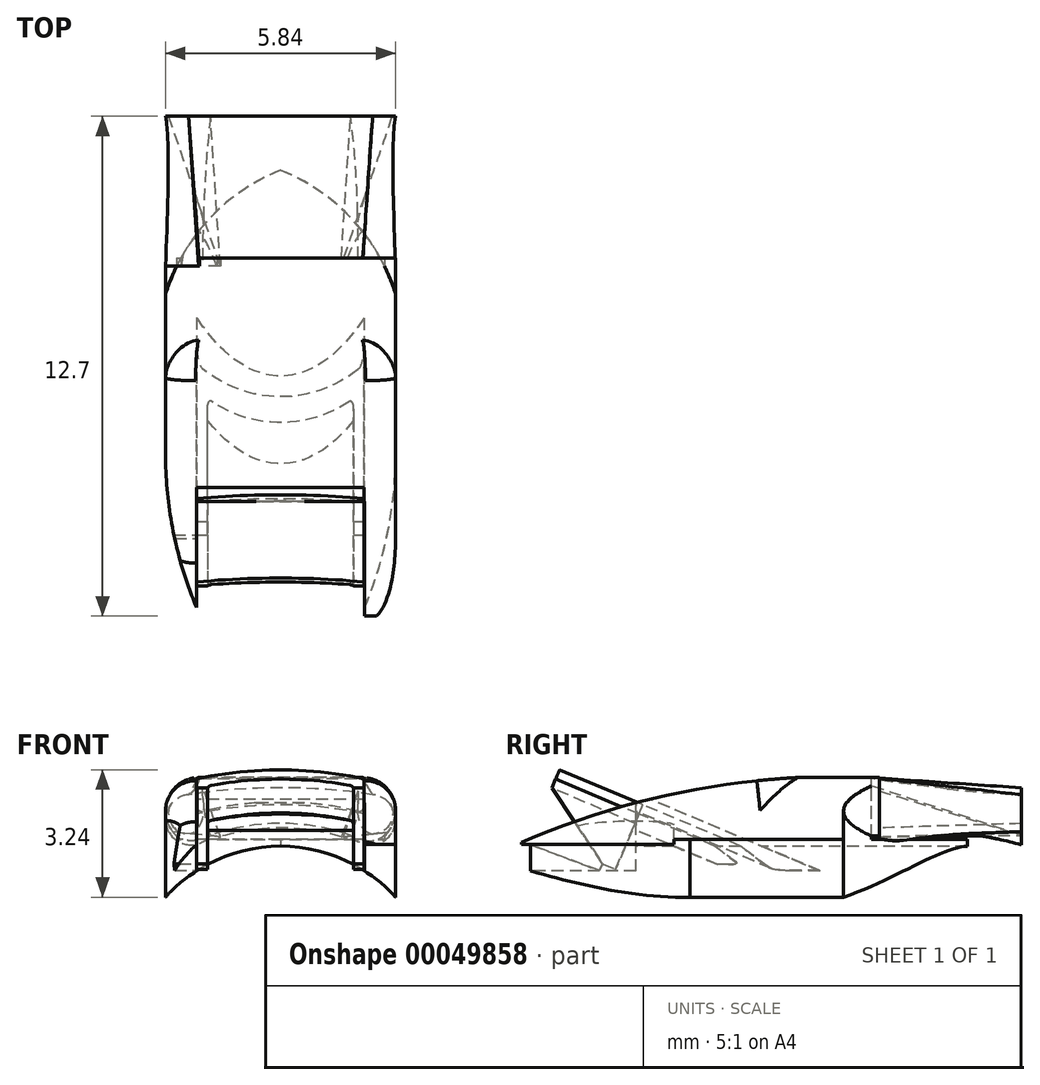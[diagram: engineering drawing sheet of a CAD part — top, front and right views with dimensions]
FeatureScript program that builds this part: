
annotation { "Feature Type Name" : "Feature", "Feature Type Description" : "" }
export const myFeature = defineFeature(function(context is Context, id is Id, definition is map)
    precondition{}
    {
        {
            var Q0;
            Q0=qCreatedBy(makeId("Front.planeOp"),FACE);
            var sketch = newSketch(context, id + "F0", { "sketchPlane" : qUnion([Q0])});
            skCircle(sketch, "E0", {"center": v(0, 0) * mm, "radius": 3.94 * mm});
            skSolve(sketch);
        }
        {
            var Q0;
            Q0=qCreatedBy(makeId("Top.planeOp"),FACE);
            cPlane(context, id + "F1", {"entities" : qUnion([Q0]), "cplaneType" : CPlaneType.OFFSET, "offset" : 2.84 * mm, "width" : 152.4 * mm, "height" : 152.4 * mm});
        }
        {
            var Q0;
            Q0=qCreatedBy(id+"F1.planeOp",FACE);
            var sketch = newSketch(context, id + "F2", { "sketchPlane" : qUnion([Q0])});
            skLineSegment(sketch, "E1", {"start": v(-2.04, 0) * mm, "end": v(2.04, 0) * mm});
            skLineSegment(sketch, "E2", {"start": v(0, 8.17) * mm, "end": v(0, 11.33) * mm});
            skArc(sketch, "E3", {"start": v(0, 11.33) * mm, "mid": v(-1.82, 10.09) * mm, "end": v(-2.92, 8.17) * mm});
            skArc(sketch, "E4.MirrorCS", {"start": v(0, 11.33) * mm, "mid": v(1.82, 10.09) * mm, "end": v(2.92, 8.17) * mm});
            skArc(sketch, "E5", {"start": v(-2.92, 4.28) * mm, "mid": v(-2.71, 2.1) * mm, "end": v(-2.04, 0) * mm});
            skArc(sketch, "E6.MirrorCS", {"start": v(2.92, 4.28) * mm, "mid": v(2.71, 2.1) * mm, "end": v(2.04, 0) * mm});
            skLineSegment(sketch, "E7", {"start": v(-2.92, 4.28) * mm, "end": v(-2.92, 8.17) * mm});
            skLineSegment(sketch, "E8", {"start": v(2.92, 4.28) * mm, "end": v(2.92, 8.17) * mm});
            skSolve(sketch);
        }
        {
            var Q0;
            Q0 = qSketchRegion(id + "F2", true);
            extrude(context, id + "F3", {"entities" : qUnion([Q0]), "depth" : 1.27 * mm, "offsetDistance" : 25.4 * mm});
        }
        {
            var Q0;
            Q0=qCreatedBy(makeId("Front.planeOp"),FACE);
            var sketch = newSketch(context, id + "F4", { "sketchPlane" : qUnion([Q0])});
            skLineSegment(sketch, "E9.bottom", {"start": v(2.92, 3.98) * mm, "end": v(-2.92, 3.98) * mm});
            skLineSegment(sketch, "E9.top", {"start": v(2.92, 5.68) * mm, "end": v(-2.92, 5.68) * mm});
            skLineSegment(sketch, "E9.left", {"start": v(2.92, 3.98) * mm, "end": v(2.92, 5.68) * mm});
            skLineSegment(sketch, "E9.right", {"start": v(-2.92, 3.98) * mm, "end": v(-2.92, 5.68) * mm});
            skPoint(sketch, "E9.middle", {"position": v(0, 4.83) * mm});
            skLineSegment(sketch, "E10", {"start": v(0, 3.98) * mm, "end": v(0, 2.84) * mm});
            skSolve(sketch);
        }
        {
            var Q0;
            Q0 = qSketchRegion(id + "F4", true);
            extrude(context, id + "F5", {"entities" : qUnion([Q0]), "oppositeDirection" : true, "depth" : 8.9 * mm, "offsetDistance" : 25.4 * mm});
        }
        {
            var Q0;
            Q0=makeQuery(id+"F5.opExtrude","CAP_FACE",FACE,{"disambiguationData":[OSD([sQuery(id+"F4.wireOp",EDGE,"E9.bottom"),sQuery(id+"F4.wireOp",EDGE,"E9.top"),sQuery(id+"F4.wireOp",EDGE,"E9.left"),sQuery(id+"F4.wireOp",EDGE,"E9.right")])],"isStart":false});
            var sketch = newSketch(context, id + "F6", { "sketchPlane" : qUnion([Q0])});
            skLineSegment(sketch, "E11.bottom", {"start": v(2.92, 3.98) * mm, "end": v(-2.92, 3.98) * mm});
            skLineSegment(sketch, "E11.top", {"start": v(2.92, 5.68) * mm, "end": v(-2.92, 5.68) * mm});
            skLineSegment(sketch, "E11.left", {"start": v(2.92, 3.98) * mm, "end": v(2.92, 5.68) * mm});
            skLineSegment(sketch, "E11.right", {"start": v(-2.92, 3.98) * mm, "end": v(-2.92, 5.68) * mm});
            skPoint(sketch, "E11.middle", {"position": v(0, 4.83) * mm});
            skLineSegment(sketch, "E12", {"start": v(0, 3.98) * mm, "end": v(0, 2.84) * mm});
            skLineSegment(sketch, "E13", {"start": v(-2.92, 4.83) * mm, "end": v(-4.23, 4.85) * mm});
            skLineSegment(sketch, "E14", {"start": v(-2.92, 3.98) * mm, "end": v(-3.64, 3.98) * mm});
            skLineSegment(sketch, "E15", {"start": v(-3.64, 3.98) * mm, "end": v(-3.64, 4.84) * mm});
            skLineSegment(sketch, "E16", {"start": v(-3.64, 4.4) * mm, "end": v(-3.33, 4.4) * mm});
            skLineSegment(sketch, "E17", {"start": v(-3.33, 4.4) * mm, "end": v(-3.33, 3.98) * mm});
            skLineSegment(sketch, "E18", {"start": v(-2.92, 5.68) * mm, "end": v(-3.33, 5.68) * mm});
            skLineSegment(sketch, "E19", {"start": v(-2.34, 5.68) * mm, "end": v(-2.34, 5.68) * mm});
            skArc(sketch, "E20", {"start": v(-2.06, 5.68) * mm, "mid": v(-2.87, 4.54) * mm, "end": v(-1.53, 4.17) * mm});
            skArc(sketch, "E21", {"start": v(1.53, 4.17) * mm, "mid": v(2.87, 4.54) * mm, "end": v(2.06, 5.68) * mm});
            skArc(sketch, "E22", {"start": v(1.53, 4.17) * mm, "mid": v(0, 4.4) * mm, "end": v(-1.53, 4.17) * mm});
            skLineSegment(sketch, "E23", {"start": v(1.53, 4.17) * mm, "end": v(2.06, 5.68) * mm});
            skLineSegment(sketch, "E24", {"start": v(-1.53, 4.17) * mm, "end": v(-2.06, 5.68) * mm});
            skSolve(sketch);
        }
        {
            var Q0;
            Q0=makeQuery(id+"F2.imprint","IMPRINT",FACE,{"disambiguationData":[TD([[makeQuery(id+"F2.imprint","IMPRINT",EDGE,{"derivedFrom":sQuery(id+"F2.wireOp",EDGE,"E1")}),1.0]])]});
            extrude(context, id + "F7", {"entities" : qUnion([Q0]), "operationType" : NewBodyOperationType.ADD, "oppositeDirection" : true, "depth" : 0.25 * mm, "offsetDistance" : 25.4 * mm});
        }
        {
            var Q0;
            Q0=qCreatedBy(makeId("Front.planeOp"),FACE);
            cPlane(context, id + "F8", {"entities" : qUnion([Q0]), "cplaneType" : CPlaneType.OFFSET, "offset" : 12.7 * mm, "oppositeDirection" : true, "width" : 152.4 * mm, "height" : 152.4 * mm});
        }
        {
            var Q0;
            Q0=qCreatedBy(id+"F8.planeOp",FACE);
            var sketch = newSketch(context, id + "F9", { "sketchPlane" : qUnion([Q0])});
            skArc(sketch, "E25", {"start": v(-2.34, 5.24) * mm, "mid": v(-2.84, 4.3) * mm, "end": v(-1.78, 4.21) * mm});
            skArc(sketch, "E26.MirrorC", {"start": v(2.41, 5.23) * mm, "mid": v(2.82, 4.27) * mm, "end": v(1.78, 4.21) * mm});
            skArc(sketch, "E27", {"start": v(1.78, 4.21) * mm, "mid": v(0, 4.51) * mm, "end": v(-1.78, 4.21) * mm});
            skLineSegment(sketch, "E28", {"start": v(0, 4.51) * mm, "end": v(0, 3.97) * mm});
            skArc(sketch, "E29", {"start": v(2.41, 5.23) * mm, "mid": v(0.04, 5.42) * mm, "end": v(-2.34, 5.24) * mm});
            skLineSegment(sketch, "E30", {"start": v(-1.78, 4.21) * mm, "end": v(-2.34, 5.24) * mm});
            skLineSegment(sketch, "E31", {"start": v(1.78, 4.21) * mm, "end": v(2.41, 5.23) * mm});
            skSolve(sketch);
        }
        {
            var Q0;
            {var subQ5=sQuery(id+"F6.wireOp",EDGE,"E23");Q0=makeQuery(id+"F6.imprint","IMPRINT",FACE,{"disambiguationData":[TD([[makeQuery(id+"F6.imprint","IMPRINT",EDGE,{"derivedFrom":subQ5}),-1.0]])]});}
            var Q1;
            Q1=makeQuery(id+"F9.imprint","IMPRINT",FACE,{"disambiguationData":[TD([[makeQuery(id+"F9.imprint","IMPRINT",EDGE,{"derivedFrom":sQuery(id+"F9.wireOp",EDGE,"E25")}),1.0]])]});
            loft(context, id + "F10", {"sheetProfilesArray" : [{ "sheetProfileEntities" : qUnion([Q0]) }, { "sheetProfileEntities" : qUnion([Q1]) }]});
        }
        {
            var Q0;
            Q0=makeQuery(id+"F6.imprint","IMPRINT",FACE,{"disambiguationData":[TD([[makeQuery(id+"F6.imprint","IMPRINT",EDGE,{"derivedFrom":sQuery(id+"F6.wireOp",EDGE,"E22")}),-1.0]])]});
            var Q1;
            Q1=makeQuery(id+"F9.imprint","IMPRINT",FACE,{"disambiguationData":[TD([[makeQuery(id+"F9.imprint","IMPRINT",EDGE,{"derivedFrom":sQuery(id+"F9.wireOp",EDGE,"E29")}),1.0]])]});
            loft(context, id + "F11", {"sheetProfilesArray" : [{ "sheetProfileEntities" : qUnion([Q0]) }, { "sheetProfileEntities" : qUnion([Q1]) }]});
        }
        {
            var Q0;
            {var subQ5=sQuery(id+"F6.wireOp",EDGE,"E23");Q0=makeQuery(id+"F10.opLoft","SWEPT_BODY",BODY,{"disambiguationData":[OSD([makeQuery(id+"F6.imprint","IMPRINT",FACE,{"disambiguationData":[TD([[makeQuery(id+"F6.imprint","IMPRINT",EDGE,{"derivedFrom":subQ5}),-1.0]])]}),makeQuery(id+"F9.imprint","IMPRINT",FACE,{"disambiguationData":[TD([[makeQuery(id+"F9.imprint","IMPRINT",EDGE,{"derivedFrom":sQuery(id+"F9.wireOp",EDGE,"E25")}),1.0]])]})])]});}
            var Q1;
            Q1=qCreatedBy(makeId("Right.planeOp"),FACE);
            mirror(context, id + "F12", {"entities" : qUnion([Q0]), "mirrorPlane" : qUnion([Q1])});
        }
        {
            var Q0;
            Q0=qCreatedBy(makeId("Right.planeOp"),FACE);
            var sketch = newSketch(context, id + "F13", { "sketchPlane" : qUnion([Q0])});
            skArc(sketch, "E32", {"start": v(8.87, 5.7) * mm, "mid": v(4.34, 5.36) * mm, "end": v(0, 4.03) * mm});
            skLineSegment(sketch, "E33", {"start": v(8.87, 5.7) * mm, "end": v(-0.3, 5.7) * mm});
            skLineSegment(sketch, "E34", {"start": v(-0.3, 5.7) * mm, "end": v(-0.3, 4.03) * mm});
            skLineSegment(sketch, "E35", {"start": v(-0.3, 4.03) * mm, "end": v(0, 4.03) * mm});
            skSolve(sketch);
        }
        {
            var Q0;
            Q0 = qSketchRegion(id + "F13", true);
            extrude(context, id + "F14", {"entities" : qUnion([Q0]), "operationType" : NewBodyOperationType.REMOVE, "depth" : 25.4 * mm, "offsetDistance" : 25.4 * mm, "symmetric" : true});
        }
        {
            var Q0;
            Q0=makeQuery(id+"F5.opExtrude","SWEPT_FACE",FACE,{"disambiguationData":[OSD([sQuery(id+"F4.wireOp",EDGE,"E9.top")])]});
            var sketch = newSketch(context, id + "F15", { "sketchPlane" : qUnion([Q0])});
            skArc(sketch, "E36", {"start": v(-2.64, 8.9) * mm, "mid": v(-2.8, 8.54) * mm, "end": v(-2.92, 8.17) * mm});
            skArc(sketch, "E37.MirrorCS", {"start": v(2.64, 8.89) * mm, "mid": v(2.8, 8.54) * mm, "end": v(2.92, 8.17) * mm});
            skArc(sketch, "E38", {"start": v(-2.92, 4.28) * mm, "mid": v(-2.71, 2.1) * mm, "end": v(-2.04, 0) * mm});
            skArc(sketch, "E39.MirrorCS", {"start": v(2.92, 4.28) * mm, "mid": v(2.71, 2.1) * mm, "end": v(2.04, 0) * mm});
            skLineSegment(sketch, "E40", {"start": v(2.92, 4.28) * mm, "end": v(3.2, 4.17) * mm});
            skLineSegment(sketch, "E41", {"start": v(3.2, 4.17) * mm, "end": v(3.2, -0.35) * mm});
            skLineSegment(sketch, "E42", {"start": v(3.2, -0.35) * mm, "end": v(2.04, -0.35) * mm});
            skLineSegment(sketch, "E43", {"start": v(2.04, -0.35) * mm, "end": v(2.04, 0) * mm});
            skLineSegment(sketch, "E44", {"start": v(-2.92, 4.28) * mm, "end": v(-3.5, 4.28) * mm});
            skLineSegment(sketch, "E45", {"start": v(-3.5, 4.28) * mm, "end": v(-3.5, -0.35) * mm});
            skLineSegment(sketch, "E46", {"start": v(-3.5, -0.35) * mm, "end": v(-2.04, -0.35) * mm});
            skLineSegment(sketch, "E47", {"start": v(-2.04, -0.35) * mm, "end": v(-2.04, 0) * mm});
            skLineSegment(sketch, "E48", {"start": v(2.64, 8.9) * mm, "end": v(2.92, 8.9) * mm});
            skLineSegment(sketch, "E49", {"start": v(2.92, 8.9) * mm, "end": v(2.92, 8.17) * mm});
            skLineSegment(sketch, "E50", {"start": v(-2.64, 8.9) * mm, "end": v(-2.92, 8.9) * mm});
            skLineSegment(sketch, "E51", {"start": v(-2.92, 8.9) * mm, "end": v(-2.92, 8.17) * mm});
            skSolve(sketch);
        }
        {
            var Q0;
            Q0=makeQuery(id+"F15.imprint","IMPRINT",FACE,{"disambiguationData":[TD([[makeQuery(id+"F15.imprint","IMPRINT",EDGE,{"derivedFrom":sQuery(id+"F15.wireOp",EDGE,"E38")}),-1.0]])]});
            var Q1;
            Q1=makeQuery(id+"F15.imprint","IMPRINT",FACE,{"disambiguationData":[TD([[makeQuery(id+"F15.imprint","IMPRINT",EDGE,{"derivedFrom":sQuery(id+"F15.wireOp",EDGE,"E39.MirrorCS")}),1.0]])]});
            var Q2;
            {var subQ0=sQuery(id+"F15.wireOp",EDGE,"E51");Q2=makeQuery(id+"F15.imprint","IMPRINT",FACE,{"disambiguationData":[TD([[makeQuery(id+"F15.imprint","IMPRINT",EDGE,{"derivedFrom":subQ0}),1.0]])]});}
            var Q3;
            {var subQ0=sQuery(id+"F15.wireOp",EDGE,"E49");Q3=makeQuery(id+"F15.imprint","IMPRINT",FACE,{"disambiguationData":[TD([[makeQuery(id+"F15.imprint","IMPRINT",EDGE,{"derivedFrom":subQ0}),-1.0]])]});}
            extrude(context, id + "F16", {"entities" : qUnion([Q0, Q1, Q2, Q3]), "operationType" : NewBodyOperationType.REMOVE, "oppositeDirection" : true, "depth" : 1.78 * mm, "offsetDistance" : 25.4 * mm});
        }
        {
            var Q0;
            Q0=makeQuery(id+"F0.imprint","IMPRINT",FACE,{"disambiguationData":[TD([[makeQuery(id+"F0.imprint","IMPRINT",EDGE,{"derivedFrom":sQuery(id+"F0.wireOp",EDGE,"E0")}),1.0]])]});
            extrude(context, id + "F17", {"entities" : qUnion([Q0]), "operationType" : NewBodyOperationType.REMOVE, "oppositeDirection" : true, "depth" : 25.4 * mm, "offsetDistance" : 25.4 * mm});
        }
        {
            var Q0;
            Q0=makeQuery(id+"F5.opExtrude","SWEPT_EDGE",EDGE,{"disambiguationData":[OSD([sQuery(id+"F4.wireOp",EDGE,"E9.top"),sQuery(id+"F4.wireOp",EDGE,"E9.right")])]});
            var Q1;
            Q1=makeQuery(id+"F5.opExtrude","SWEPT_EDGE",EDGE,{"disambiguationData":[OSD([sQuery(id+"F4.wireOp",EDGE,"E9.top"),sQuery(id+"F4.wireOp",EDGE,"E9.left")])]});
            fillet(context, id + "F18", {"entities" : qUnion([Q0, Q1]), "tangentPropagation" : true, "radius" : 0.84 * mm, "defaultsChanged" : false, "vertexSettings" : [], "allowEdgeOverflow" : false});
        }
        {
            var Q0;
            {var subQ0=sQuery(id+"F4.wireOp",EDGE,"E9.right");var subQ2=sQuery(id+"F4.wireOp",EDGE,"E9.top");var subQ3=sQuery(id+"F13.wireOp",EDGE,"E32");Q0=makeQuery(id+"F18.opFillet","BLEND_EDGE",EDGE,{"blendedFrom":[makeQuery(id+"F5.opExtrude","SWEPT_EDGE",EDGE,{"disambiguationData":[OSD([subQ2,subQ0])]}),makeQuery(id+"F14.boolean.opBoolean","COPY",FACE,{"disambiguationData":[TD([makeQuery(id+"F5.opExtrude","SWEPT_FACE",FACE,{"disambiguationData":[OSD([subQ2])]})])],"derivedFrom":makeQuery(id+"F14.opExtrude","SWEPT_FACE",FACE,{"disambiguationData":[OSD([subQ3]),TDD([makeQuery(id+"F13.imprint","IMPRINT",EDGE,{"disambiguationData":[TD([[makeQuery(id+"F13.imprint","INTERSECT",VERTEX,{"derivedFrom":[subQ3,sQuery(id+"F13.wireOp",EDGE,"E35")]}),1.0]])],"derivedFrom":subQ3})])]})})],"blendedInto":[makeQuery(id+"F14.boolean.opBoolean","COPY",FACE,{"disambiguationData":[TD([makeQuery(id+"F5.opExtrude","SWEPT_FACE",FACE,{"disambiguationData":[OSD([subQ2])]})])],"derivedFrom":makeQuery(id+"F14.opExtrude","SWEPT_FACE",FACE,{"disambiguationData":[OSD([subQ3]),TDD([makeQuery(id+"F13.imprint","IMPRINT",EDGE,{"disambiguationData":[TD([[makeQuery(id+"F13.imprint","INTERSECT",VERTEX,{"derivedFrom":[subQ3,sQuery(id+"F13.wireOp",EDGE,"E35")]}),1.0]])],"derivedFrom":subQ3})])]})})]});}
            fillet(context, id + "F19", {"entities" : qUnion([Q0]), "tangentPropagation" : true, "radius" : 0.76 * mm, "defaultsChanged" : true, "vertexSettings" : [], "allowEdgeOverflow" : false});
        }
        {
            var Q0;
            Q0=makeQuery(id+"F5.opExtrude","SWEPT_FACE",FACE,{"disambiguationData":[OSD([sQuery(id+"F4.wireOp",EDGE,"E9.bottom")])]});
            var sketch = newSketch(context, id + "F20", { "sketchPlane" : qUnion([Q0])});
            skArc(sketch, "E52", {"start": v(2.64, -8.89) * mm, "mid": v(2.8, -8.54) * mm, "end": v(2.92, -8.17) * mm});
            skArc(sketch, "E53.MirrorCS", {"start": v(-2.64, -8.89) * mm, "mid": v(-2.8, -8.54) * mm, "end": v(-2.92, -8.17) * mm});
            skLineSegment(sketch, "E54", {"start": v(-2.64, -8.89) * mm, "end": v(-2.92, -8.89) * mm});
            skLineSegment(sketch, "E55", {"start": v(-2.92, -8.89) * mm, "end": v(-2.92, -8.17) * mm});
            skLineSegment(sketch, "E56", {"start": v(2.64, -8.89) * mm, "end": v(2.92, -8.89) * mm});
            skLineSegment(sketch, "E57", {"start": v(2.92, -8.89) * mm, "end": v(2.92, -8.17) * mm});
            skSolve(sketch);
        }
        {
            var Q0;
            {var subQ0=sQuery(id+"F20.wireOp",EDGE,"E56");Q0=makeQuery(id+"F20.imprint","IMPRINT",FACE,{"disambiguationData":[TD([[makeQuery(id+"F20.imprint","IMPRINT",EDGE,{"derivedFrom":subQ0}),1.0]])]});}
            var Q1;
            {var subQ0=sQuery(id+"F20.wireOp",EDGE,"E54");Q1=makeQuery(id+"F20.imprint","IMPRINT",FACE,{"disambiguationData":[TD([[makeQuery(id+"F20.imprint","IMPRINT",EDGE,{"derivedFrom":subQ0}),-1.0]])]});}
            extrude(context, id + "F21", {"entities" : qUnion([Q0, Q1]), "operationType" : NewBodyOperationType.REMOVE, "oppositeDirection" : true, "depth" : 2.74 * mm, "offsetDistance" : 25.4 * mm});
        }
        {
            var Q0;
            {var subQ5=sQuery(id+"F6.wireOp",EDGE,"E23");Q0=makeQuery(id+"F6.imprint","IMPRINT",FACE,{"disambiguationData":[TD([[makeQuery(id+"F6.imprint","IMPRINT",EDGE,{"derivedFrom":subQ5}),-1.0]])]});}
            var Q1;
            {var subQ0=sQuery(id+"F6.wireOp",EDGE,"E24");Q1=makeQuery(id+"F6.imprint","IMPRINT",FACE,{"disambiguationData":[TD([[makeQuery(id+"F6.imprint","IMPRINT",EDGE,{"derivedFrom":subQ0}),1.0]])]});}
            extrude(context, id + "F22", {"entities" : qUnion([Q0, Q1]), "oppositeDirection" : true, "depth" : 1.27 * mm, "offsetDistance" : 25.4 * mm});
        }
        {
            var Q0;
            Q0=makeQuery(id+"F3.opExtrude","SWEPT_BODY",BODY,{"disambiguationData":[OSD([sQuery(id+"F2.wireOp",EDGE,"E1"),sQuery(id+"F2.wireOp",EDGE,"E3"),sQuery(id+"F2.wireOp",EDGE,"E4.MirrorCS"),sQuery(id+"F2.wireOp",EDGE,"E5"),sQuery(id+"F2.wireOp",EDGE,"E6.MirrorCS"),sQuery(id+"F2.wireOp",EDGE,"E7"),sQuery(id+"F2.wireOp",EDGE,"E8")])]});
            var Q1;
            Q1=makeQuery(id+"F5.opExtrude","SWEPT_BODY",BODY,{"disambiguationData":[OSD([sQuery(id+"F4.wireOp",EDGE,"E9.bottom"),sQuery(id+"F4.wireOp",EDGE,"E9.top"),sQuery(id+"F4.wireOp",EDGE,"E9.left"),sQuery(id+"F4.wireOp",EDGE,"E9.right")])]});
            var Q2;
            Q2=makeQuery(id+"F22.opExtrude","SWEPT_BODY",BODY,{"disambiguationData":[OSD([sQuery(id+"F6.wireOp",EDGE,"E11.top"),sQuery(id+"F6.wireOp",EDGE,"E20"),sQuery(id+"F6.wireOp",EDGE,"E24")])]});
            var Q3;
            {var subQ5=sQuery(id+"F6.wireOp",EDGE,"E23");Q3=makeQuery(id+"F10.opLoft","SWEPT_BODY",BODY,{"disambiguationData":[OSD([makeQuery(id+"F6.imprint","IMPRINT",FACE,{"disambiguationData":[TD([[makeQuery(id+"F6.imprint","IMPRINT",EDGE,{"derivedFrom":subQ5}),-1.0]])]}),makeQuery(id+"F9.imprint","IMPRINT",FACE,{"disambiguationData":[TD([[makeQuery(id+"F9.imprint","IMPRINT",EDGE,{"derivedFrom":sQuery(id+"F9.wireOp",EDGE,"E25")}),1.0]])]})])]});}
            var Q4;
            Q4=makeQuery(id+"F22.opExtrude","SWEPT_BODY",BODY,{"disambiguationData":[OSD([sQuery(id+"F6.wireOp",EDGE,"E11.top"),sQuery(id+"F6.wireOp",EDGE,"E21"),sQuery(id+"F6.wireOp",EDGE,"E23")])]});
            booleanBodies(context, id + "F23", {"operationType" : BooleanOperationType.UNION, "tools" : qUnion([Q0, Q1, Q2, Q3, Q4])});
        }
        {
            var Q0;
            Q0=makeQuery(id+"F5.opExtrude","SWEPT_FACE",FACE,{"disambiguationData":[OSD([sQuery(id+"F4.wireOp",EDGE,"E9.top")])]});
            var sketch = newSketch(context, id + "F24", { "sketchPlane" : qUnion([Q0])});
            skLineSegment(sketch, "E58", {"start": v(-2.14, 2.9) * mm, "end": v(-2.14, 0) * mm});
            skLineSegment(sketch, "E59.MirrorCS", {"start": v(2.14, 2.9) * mm, "end": v(2.14, 0) * mm});
            skLineSegment(sketch, "E60", {"start": v(-2.14, 0) * mm, "end": v(2.14, 0) * mm});
            skLineSegment(sketch, "E61", {"start": v(-2.14, 2.9) * mm, "end": v(2.14, 2.9) * mm});
            skSolve(sketch);
        }
        {
            var Q0;
            Q0 = qSketchRegion(id + "F24", true);
            extrude(context, id + "F25", {"entities" : qUnion([Q0]), "operationType" : NewBodyOperationType.REMOVE, "oppositeDirection" : true, "depth" : 25.4 * mm, "offsetDistance" : 25.4 * mm});
        }
        {
            var Q0;
            Q0=qCreatedBy(makeId("Right.planeOp"),FACE);
            var sketch = newSketch(context, id + "F26", { "sketchPlane" : qUnion([Q0])});
            skLineSegment(sketch, "E62", {"start": v(0.49, 5.8) * mm, "end": v(4.49, 4.12) * mm});
            skSolve(sketch);
        }
        {
            var Q0;
            Q0=sQuery(id+"F26.wireOp",EDGE,"E62");
            cPlane(context, id + "F27", {"entities" : qUnion([Q0]), "cplaneType" : CPlaneType.LINE_ANGLE, "offset" : 25.4 * mm, "angle" : 0 * degree, "width" : 152.4 * mm, "height" : 152.4 * mm});
        }
        {
            var Q0;
            Q0=qCreatedBy(id+"F27.planeOp",FACE);
            var sketch = newSketch(context, id + "F28", { "sketchPlane" : qUnion([Q0])});
            skLineSegment(sketch, "E63", {"start": v(2.12, -1.39) * mm, "end": v(-2.13, -1.39) * mm});
            skLineSegment(sketch, "E64", {"start": v(2.12, -1.39) * mm, "end": v(2.12, 0.9) * mm});
            skLineSegment(sketch, "E65", {"start": v(2.12, 0.9) * mm, "end": v(-2.13, 0.9) * mm});
            skLineSegment(sketch, "E66", {"start": v(-2.13, 0.9) * mm, "end": v(-2.13, -1.39) * mm});
            skSolve(sketch);
        }
        {
            var Q0;
            Q0 = qSketchRegion(id + "F28", true);
            extrude(context, id + "F29", {"entities" : qUnion([Q0]), "depth" : 0.5 * mm, "offsetDistance" : 25.4 * mm, "symmetric" : true});
        }
        {
            var Q0;
            Q0=makeQuery(id+"F29.opExtrude","SWEPT_FACE",FACE,{"disambiguationData":[OSD([sQuery(id+"F28.wireOp",EDGE,"E63")])]});
            var sketch = newSketch(context, id + "F30", { "sketchPlane" : qUnion([Q0])});
            skLineSegment(sketch, "E67", {"start": v(2.12, 5.54) * mm, "end": v(2.12, 5.54) * mm});
            skArc(sketch, "E68", {"start": v(2.12, 5.54) * mm, "mid": v(0, 5.8) * mm, "end": v(-2.13, 5.54) * mm});
            skLineSegment(sketch, "E69", {"start": v(-2.13, 5.54) * mm, "end": v(-2.13, 6) * mm});
            skLineSegment(sketch, "E70", {"start": v(-2.13, 6) * mm, "end": v(2.12, 6) * mm});
            skLineSegment(sketch, "E71", {"start": v(2.12, 6) * mm, "end": v(2.12, 5.54) * mm});
            skArc(sketch, "E72", {"start": v(1.86, 5.34) * mm, "mid": v(0, 5.54) * mm, "end": v(-1.86, 5.34) * mm});
            skLineSegment(sketch, "E73", {"start": v(-1.86, 5.13) * mm, "end": v(1.86, 5.13) * mm});
            skLineSegment(sketch, "E74", {"start": v(-1.86, 5.13) * mm, "end": v(-1.86, 5.34) * mm});
            skLineSegment(sketch, "E75", {"start": v(1.86, 5.13) * mm, "end": v(1.86, 5.34) * mm});
            skSolve(sketch);
        }
        {
            var Q0;
            Q0 = qSketchRegion(id + "F30", true);
            extrude(context, id + "F31", {"entities" : qUnion([Q0]), "operationType" : NewBodyOperationType.REMOVE, "oppositeDirection" : true, "depth" : 25.4 * mm, "offsetDistance" : 25.4 * mm});
        }
        {
            var Q0;
            Q0=makeQuery(id+"F29.opExtrude","CAP_FACE",FACE,{"disambiguationData":[OSD([sQuery(id+"F28.wireOp",EDGE,"jt4GWxga-MMcO-UU4e-7Edf-iDZYVW5mtqn9"),sQuery(id+"F28.wireOp",EDGE,"E63"),sQuery(id+"F28.wireOp",EDGE,"brbIYKwW-AIyR-SsEO-6SLP-HjVVP1DYZ7g1"),sQuery(id+"F28.wireOp",EDGE,"CK7rohKX-ZbzJ-NtJX-0UGZ-hewyezXCtVgG")])],"isStart":true});
            var sketch = newSketch(context, id + "F32", { "sketchPlane" : qUnion([Q0])});
            skLineSegment(sketch, "E76", {"start": v(0, 1.39) * mm, "end": v(0, 0.2) * mm});
            skLineSegment(sketch, "E77.MirrorCS", {"start": v(-2.39, -0.72) * mm, "end": v(-2.39, 1.39) * mm});
            skLineSegment(sketch, "E78.MirrorCS", {"start": v(1.86, 1.39) * mm, "end": v(2.12, 1.39) * mm});
            skLineSegment(sketch, "E79.MirrorCS", {"start": v(-1.86, 1.39) * mm, "end": v(-2.12, 1.39) * mm});
            skLineSegment(sketch, "E80", {"start": v(2.12, 1.39) * mm, "end": v(2.12, -0.9) * mm});
            skLineSegment(sketch, "E81", {"start": v(2.12, -0.9) * mm, "end": v(1.86, -0.9) * mm});
            skLineSegment(sketch, "E82", {"start": v(1.86, -0.9) * mm, "end": v(1.86, 1.39) * mm});
            skLineSegment(sketch, "E83", {"start": v(-1.86, 1.39) * mm, "end": v(-1.86, -0.9) * mm});
            skLineSegment(sketch, "E84", {"start": v(-1.86, -0.9) * mm, "end": v(-2.13, -0.9) * mm});
            skLineSegment(sketch, "E85", {"start": v(-2.13, -0.9) * mm, "end": v(-2.12, 1.39) * mm});
            skSolve(sketch);
        }
        {
            var Q0;
            Q0 = qSketchRegion(id + "F32", true);
            extrude(context, id + "F33", {"entities" : qUnion([Q0]), "operationType" : NewBodyOperationType.ADD, "depth" : 1.27 * mm, "offsetDistance" : 25.4 * mm});
        }
        {
            var Q0;
            Q0=makeQuery(id+"F31.boolean.opBoolean","COPY",EDGE,{"derivedFrom":makeQuery(id+"F31.opExtrude","SWEPT_EDGE",EDGE,{"disambiguationData":[OSD([sQuery(id+"F28.wireOp",EDGE,"E63"),sQuery(id+"F28.wireOp",EDGE,"E66"),sQuery(id+"F30.wireOp",EDGE,"E68"),sQuery(id+"F30.wireOp",EDGE,"E69")])]})});
            var Q1;
            Q1=makeQuery(id+"F31.boolean.opBoolean","COPY",EDGE,{"derivedFrom":makeQuery(id+"F31.opExtrude","SWEPT_EDGE",EDGE,{"disambiguationData":[OSD([sQuery(id+"F28.wireOp",EDGE,"E63"),sQuery(id+"F28.wireOp",EDGE,"E64"),sQuery(id+"F30.wireOp",EDGE,"E68"),sQuery(id+"F30.wireOp",EDGE,"E71")])]})});
            var Q2;
            Q2=makeQuery(id+"F31.boolean.opBoolean","COPY",EDGE,{"derivedFrom":makeQuery(id+"F31.opExtrude","SWEPT_EDGE",EDGE,{"disambiguationData":[OSD([sQuery(id+"F30.wireOp",EDGE,"E72"),sQuery(id+"F30.wireOp",EDGE,"E74")])]})});
            var Q3;
            Q3=makeQuery(id+"F31.boolean.opBoolean","COPY",EDGE,{"derivedFrom":makeQuery(id+"F31.opExtrude","SWEPT_EDGE",EDGE,{"disambiguationData":[OSD([sQuery(id+"F30.wireOp",EDGE,"E72"),sQuery(id+"F30.wireOp",EDGE,"E75")])]})});
            fillet(context, id + "F34", {"entities" : qUnion([Q0, Q1, Q2, Q3]), "tangentPropagation" : true, "radius" : 0.13 * mm, "defaultsChanged" : false, "vertexSettings" : [], "allowEdgeOverflow" : false});
        }
        {
            var Q0;
            Q0=makeQuery(id+"F33.boolean.opBoolean","MERGE",FACE,{"derivedFrom":[makeQuery(id+"F29.opExtrude","SWEPT_FACE",FACE,{"disambiguationData":[OSD([sQuery(id+"F28.wireOp",EDGE,"E64")])]}),makeQuery(id+"F33.opExtrude","SWEPT_FACE",FACE,{"disambiguationData":[OSD([sQuery(id+"F32.wireOp",EDGE,"E80")])]})]});
            var sketch = newSketch(context, id + "F35", { "sketchPlane" : qUnion([Q0])});
            skLineSegment(sketch, "E86", {"start": v(2.4, 3.35) * mm, "end": v(2.06, 3.49) * mm});
            skLineSegment(sketch, "E87", {"start": v(2.06, 3.49) * mm, "end": v(0.77, 5.41) * mm});
            skLineSegment(sketch, "E88", {"start": v(1.98, 3.32) * mm, "end": v(2.06, 3.49) * mm});
            skLineSegment(sketch, "E89", {"start": v(0.77, 5.41) * mm, "end": v(0.67, 5.46) * mm});
            skLineSegment(sketch, "E90", {"start": v(0.67, 5.46) * mm, "end": v(0.07, 4.03) * mm});
            skLineSegment(sketch, "E91", {"start": v(0.07, 4.03) * mm, "end": v(1.98, 3.32) * mm});
            skSolve(sketch);
        }
        {
            var Q0;
            Q0 = qSketchRegion(id + "F35", true);
            extrude(context, id + "F36", {"entities" : qUnion([Q0]), "operationType" : NewBodyOperationType.REMOVE, "oppositeDirection" : true, "depth" : 25.4 * mm, "offsetDistance" : 25.4 * mm});
        }
        {
            var Q0;
            {var subQ0=sQuery(id+"F2.wireOp",EDGE,"E4.MirrorCS");Q0=makeQuery(id+"F23.opBoolean","SPLIT",FACE,{"disambiguationData":[TD([makeQuery(id+"F3.opExtrude","SWEPT_FACE",FACE,{"disambiguationData":[OSD([subQ0])]})])],"derivedFrom":makeQuery(id+"F5.opExtrude","CAP_FACE",FACE,{"disambiguationData":[OSD([sQuery(id+"F4.wireOp",EDGE,"E9.bottom"),sQuery(id+"F4.wireOp",EDGE,"E9.top"),sQuery(id+"F4.wireOp",EDGE,"E9.left"),sQuery(id+"F4.wireOp",EDGE,"E9.right")])],"isStart":false})});}
            var Q1;
            {var subQ1=sQuery(id+"F2.wireOp",EDGE,"E3");Q1=makeQuery(id+"F23.opBoolean","SPLIT",FACE,{"disambiguationData":[TD([makeQuery(id+"F3.opExtrude","SWEPT_FACE",FACE,{"disambiguationData":[OSD([subQ1])]})])],"derivedFrom":makeQuery(id+"F5.opExtrude","CAP_FACE",FACE,{"disambiguationData":[OSD([sQuery(id+"F4.wireOp",EDGE,"E9.bottom"),sQuery(id+"F4.wireOp",EDGE,"E9.top"),sQuery(id+"F4.wireOp",EDGE,"E9.left"),sQuery(id+"F4.wireOp",EDGE,"E9.right")])],"isStart":false})});}
            extrude(context, id + "F37", {"entities" : qUnion([Q0, Q1]), "operationType" : NewBodyOperationType.ADD, "depth" : 0.2 * mm, "offsetDistance" : 25.4 * mm});
        }
    });
